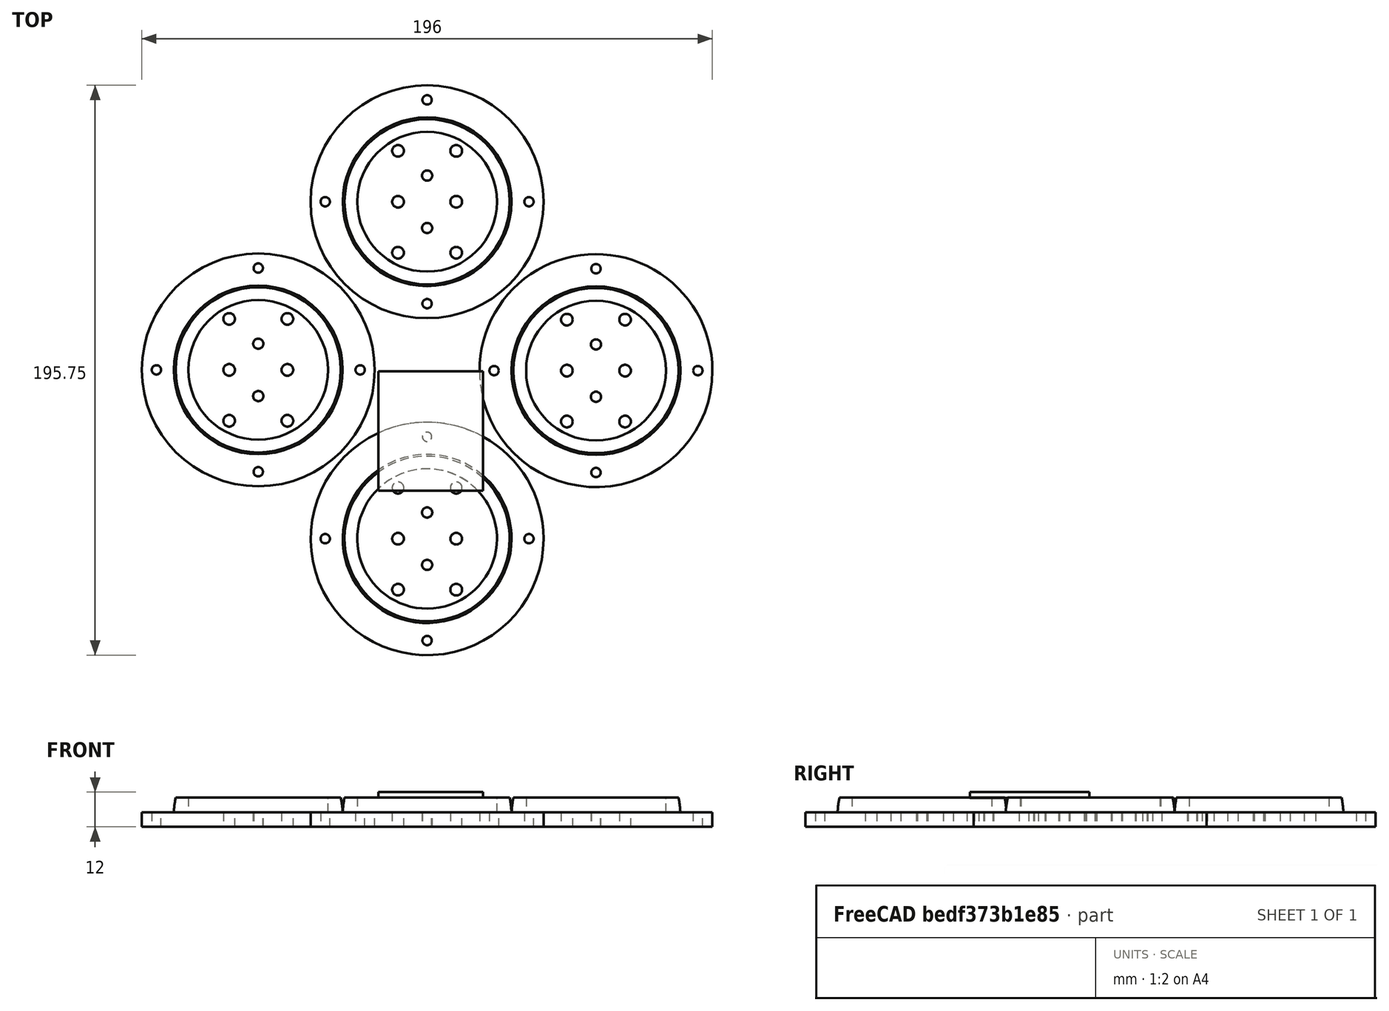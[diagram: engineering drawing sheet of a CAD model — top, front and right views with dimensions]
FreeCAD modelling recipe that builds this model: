
FCSTD DOCUMENT  (FreeCAD 0.20R29410 (Git))
Label: lightModuleV2
License: All rights reserved
LicenseURL: http://en.wikipedia.org/wiki/All_rights_reserved
objects: Part::Cylinder×56, Part::MultiFuse×32, Part::Cut×12, Part::Sphere×4, Mesh::Feature×1, Sketcher::SketchObject×1, Part::Box×1
note: 106 computed .brp shape members not serialized (recipe doc carries the construction recipe); baked Part::Feature solids carry a one-line shape summary decoded from their .brp

FEATURE [Mesh::Feature] Odroid_H004  label="Odroid-H004"
FEATURE [Sketcher::SketchObject] Sketch  label="top"
  FullyConstrained = false
  sketch-geometry (25):
    g0: Circle CenterX=0 CenterY=-150 CenterZ=0 NormalX=0 NormalY=0 NormalZ=1 AngleXU=0 Radius=100
    g1: Circle CenterX=0 CenterY=-208 CenterZ=0 NormalX=0 NormalY=0 NormalZ=1 AngleXU=0 Radius=40
    g2: Circle CenterX=58 CenterY=-150 CenterZ=0 NormalX=0 NormalY=0 NormalZ=1 AngleXU=0 Radius=40
    g3: Circle CenterX=0 CenterY=-92 CenterZ=0 NormalX=0 NormalY=0 NormalZ=1 AngleXU=0 Radius=40
    g4: Circle CenterX=-58 CenterY=-150 CenterZ=0 NormalX=0 NormalY=0 NormalZ=1 AngleXU=0 Radius=40
    g5: Circle CenterX=-93.2591 CenterY=-150.487 CenterZ=0 NormalX=0 NormalY=0 NormalZ=1 AngleXU=0 Radius=1.31835
    g6: Circle CenterX=-57.3054 CenterY=-115.377 CenterZ=0 NormalX=0 NormalY=0 NormalZ=1 AngleXU=0 Radius=2.19437
    g7: Circle CenterX=-22.8708 CenterY=-149.812 CenterZ=0 NormalX=0 NormalY=0 NormalZ=1 AngleXU=0 Radius=2.50935
    g8: Circle CenterX=-58.3181 CenterY=-186.103 CenterZ=0 NormalX=0 NormalY=0 NormalZ=1 AngleXU=0 Radius=1.8872
    g9: Circle CenterX=0 CenterY=-172.431 CenterZ=0 NormalX=0 NormalY=0 NormalZ=1 AngleXU=0 Radius=3.27743
    g10: Circle CenterX=0 CenterY=-243.157 CenterZ=0 NormalX=0 NormalY=0 NormalZ=1 AngleXU=0 Radius=1.88719
    g11: Circle CenterX=-35.1929 CenterY=-208.216 CenterZ=0 NormalX=0 NormalY=0 NormalZ=1 AngleXU=0 Radius=2.03259
    g12: Circle CenterX=35.7018 CenterY=-208.047 CenterZ=0 NormalX=0 NormalY=0 NormalZ=1 AngleXU=0 Radius=2.06044
    g13: Circle CenterX=57.8865 CenterY=-185.172 CenterZ=0 NormalX=0 NormalY=0 NormalZ=1 AngleXU=0 Radius=1.98371
    g14: Circle CenterX=23.2953 CenterY=-150.097 CenterZ=0 NormalX=0 NormalY=0 NormalZ=1 AngleXU=0 Radius=1.91236
    g15: Circle CenterX=58.0074 CenterY=-115.385 CenterZ=0 NormalX=0 NormalY=0 NormalZ=1 AngleXU=0 Radius=2.56571
    g16: Circle CenterX=93.3244 CenterY=-150.823 CenterZ=0 NormalX=0 NormalY=0 NormalZ=1 AngleXU=0 Radius=1.84224
    g17: Circle CenterX=0 CenterY=-58.0915 CenterZ=0 NormalX=0 NormalY=0 NormalZ=1 AngleXU=0 Radius=2.47929
    g18: Circle CenterX=0 CenterY=-208 CenterZ=0 NormalX=0 NormalY=0 NormalZ=1 AngleXU=0 Radius=25.6697
    g19: Circle CenterX=-58 CenterY=-150 CenterZ=0 NormalX=0 NormalY=0 NormalZ=1 AngleXU=0 Radius=24.6603
    g20: Circle CenterX=58 CenterY=-150 CenterZ=0 NormalX=0 NormalY=0 NormalZ=1 AngleXU=0 Radius=24.7378
    g21: Circle CenterX=0 CenterY=-92 CenterZ=0 NormalX=0 NormalY=0 NormalZ=1 AngleXU=0 Radius=24.1932
    g22: Circle CenterX=-35.0038 CenterY=-92.3918 CenterZ=0 NormalX=0 NormalY=0 NormalZ=1 AngleXU=0 Radius=2.19456
    g23: Circle CenterX=34.6146 CenterY=-92.5741 CenterZ=0 NormalX=0 NormalY=0 NormalZ=1 AngleXU=0 Radius=1.93732
    g24: Circle CenterX=0 CenterY=-127.201 CenterZ=0 NormalX=0 NormalY=0 NormalZ=1 AngleXU=0 Radius=2.07794
  constraints (23):
    c: PointOnObject(g0,g-2)
    c: Radius(g0) = 100
    c: DistanceY(g0) = -150
    c: PointOnObject(g1,g-2)
    c: PointOnObject(g3,g-2)
    c: DistanceY(g0,g2) = 0
    c: DistanceY(g0,g4) = 0
    c: DistanceY(g1,g0) = 58
    c: DistanceX(g4,g0) = 58
    c: DistanceX(g0,g2) = 58
    c: DistanceY(g0,g3) = 58
    c: Equal(g1,g2)
    c: Equal(g1,g3)
    c: Equal(g1,g4)
    c: Radius(g1) = 40
    c: PointOnObject(g9,g-2)
    c: PointOnObject(g10,g-2)
    c: PointOnObject(g17,g-2)
    c: Coincident(g18,g1)
    c: Coincident(g19,g4)
    c: Coincident(g20,g2)
    c: Coincident(g21,g3)
    c: PointOnObject(g24,g-2)
FEATURE [Part::Cylinder] Cylinder036
  Angle = 360
  AttacherType = Attacher::AttachEngine3D
  FirstAngle = 0
  Height = 10
  Placement = pos=(0,-21,0) rot=(0,0,1;0rad)
  Radius = 2
  SecondAngle = 0
FEATURE [Part::Cylinder] Cylinder037
  Angle = 360
  AttacherType = Attacher::AttachEngine3D
  FirstAngle = 0
  Height = 10
  Placement = pos=(20,-21,0) rot=(0,0,1;0rad)
  Radius = 2
  SecondAngle = 0
FEATURE [Part::Cylinder] Cylinder038
  Angle = 360
  AttacherType = Attacher::AttachEngine3D
  FirstAngle = 0
  Height = 10
  Placement = pos=(0,-21,0) rot=(0,0,1;0rad)
  Radius = 2
  SecondAngle = 0
FEATURE [Part::Cylinder] Cylinder039
  Angle = 360
  AttacherType = Attacher::AttachEngine3D
  FirstAngle = 0
  Height = 10
  Placement = pos=(20,-21,0) rot=(0,0,1;0rad)
  Radius = 2
  SecondAngle = 0
FEATURE [Part::Cylinder] Cylinder040  label="base002"
  Angle = 360
  AttacherType = Attacher::AttachEngine3D
  FirstAngle = 0
  Height = 5
  Placement = pos=(5,0,70) rot=(0,0,1;0rad)
  Radius = 40
  SecondAngle = 0
FEATURE [Part::Cylinder] Cylinder041  label="baseCut001"
  Angle = 360
  AttacherType = Attacher::AttachEngine3D
  FirstAngle = 0
  Height = 7
  Placement = pos=(5,0,74) rot=(0,0,1;0rad)
  Radius = 24
  SecondAngle = 0
FEATURE [Part::Cylinder] Cylinder042  label="wireCUt002"
  Angle = 360
  AttacherType = Attacher::AttachEngine3D
  FirstAngle = 0
  Height = 10
  Placement = pos=(-5,0,70) rot=(0,0,1;0rad)
  Radius = 2
  SecondAngle = 0
FEATURE [Part::Cylinder] Cylinder043  label="wireCUt003"
  Angle = 360
  AttacherType = Attacher::AttachEngine3D
  FirstAngle = 0
  Height = 10
  Placement = pos=(15,0,70) rot=(0,0,1;0rad)
  Radius = 2
  SecondAngle = 0
FEATURE [Part::Cylinder] Cylinder044  label="m3Cuts002"
  Angle = 360
  AttacherType = Attacher::AttachEngine3D
  FirstAngle = 0
  Height = 10
  Placement = pos=(5,-9,70) rot=(0,0,1;0rad)
  Radius = 1.75
  SecondAngle = 0
FEATURE [Part::Cylinder] Cylinder045  label="m3Cuts003"
  Angle = 360
  AttacherType = Attacher::AttachEngine3D
  FirstAngle = 0
  Height = 10
  Placement = pos=(5,9,70) rot=(0,0,1;0rad)
  Radius = 1.75
  SecondAngle = 0
FEATURE [Part::Cylinder] Cylinder046  label="m2HeatSetInsets004"
  Angle = 360
  AttacherType = Attacher::AttachEngine3D
  FirstAngle = 0
  Height = 10
  Placement = pos=(-30,0,65) rot=(0,0,1;0rad)
  Radius = 1.6
  SecondAngle = 0
FEATURE [Part::Cylinder] Cylinder047  label="m2HeatSetInsets005"
  Angle = 360
  AttacherType = Attacher::AttachEngine3D
  FirstAngle = 0
  Height = 10
  Placement = pos=(40,0,65) rot=(0,0,1;0rad)
  Radius = 1.6
  SecondAngle = 0
FEATURE [Part::Cylinder] Cylinder048  label="m2HeatSetInsets006"
  Angle = 360
  AttacherType = Attacher::AttachEngine3D
  FirstAngle = 0
  Height = 10
  Placement = pos=(5,35,65) rot=(0,0,1;0rad)
  Radius = 1.6
  SecondAngle = 0
FEATURE [Part::Cylinder] Cylinder049  label="m2HeatSetInsets007"
  Angle = 360
  AttacherType = Attacher::AttachEngine3D
  FirstAngle = 0
  Height = 10
  Placement = pos=(5,-35,65) rot=(0,0,1;0rad)
  Radius = 1.6
  SecondAngle = 0
FEATURE [Part::MultiFuse] Fusion014  label="m3HeatSetCuts003"
  Placement = pos=(-5,38.5,70) rot=(0,0,1;0rad)
  Shapes = -> [Cylinder037,Cylinder036]
FEATURE [Part::MultiFuse] Fusion015  label="m3HeatSetCuts004"
  Placement = pos=(-5,3.5,70) rot=(0,0,1;0rad)
  Shapes = -> [Cylinder039,Cylinder038]
FEATURE [Part::MultiFuse] Fusion016  label="m3HeatSetCuts005"
  Shapes = -> [Fusion015,Fusion014]
FEATURE [Part::MultiFuse] Fusion017  label="wireCuts001"
  Shapes = -> [Cylinder042,Cylinder043]
FEATURE [Part::MultiFuse] Fusion018  label="m3Cute001"
  Shapes = -> [Cylinder044,Cylinder045]
FEATURE [Part::MultiFuse] Fusion019  label="baseCUts001"
  Shapes = -> [Fusion016,Fusion017,Fusion018]
FEATURE [Part::MultiFuse] Fusion021
  Shapes = -> [Cylinder046,Cylinder047,Cylinder048,Cylinder049]
FEATURE [Part::Sphere] Sphere002  label="SphereBase001"
  Angle1 = 0
  Angle2 = 12
  Angle3 = 360
  AttacherType = Attacher::AttachEngine3D
  Placement = pos=(5,0,74) rot=(0,0,1;0rad)
  Radius = 29
FEATURE [Part::Cut] Cut006
  Base = -> Sphere002
  Tool = -> Cylinder041
FEATURE [Part::MultiFuse] Fusion020  label="base003"
  Shapes = -> [Cylinder040,Cut006]
FEATURE [Part::Cut] Cut007
  Base = -> Fusion020
  Tool = -> Fusion019
FEATURE [Part::Cut] Cut008  label="lightModule001"
  Base = -> Cut007
  Placement = pos=(-5,-208,0) rot=(0,1,0;0rad)
  Tool = -> Fusion021
FEATURE [Part::Box] Box005  label="as7265x"
  AttacherType = Attacher::AttachEngine3D
  Height = 2
  Length = 36
  Placement = pos=(-16.75,-191.5,80) rot=(0,0,1;0rad)
  Width = 41
FEATURE [Part::Cylinder] Cylinder050
  Angle = 360
  AttacherType = Attacher::AttachEngine3D
  FirstAngle = 0
  Height = 10
  Placement = pos=(0,-21,0) rot=(0,0,1;0rad)
  Radius = 2
  SecondAngle = 0
FEATURE [Part::Cylinder] Cylinder051
  Angle = 360
  AttacherType = Attacher::AttachEngine3D
  FirstAngle = 0
  Height = 10
  Placement = pos=(20,-21,0) rot=(0,0,1;0rad)
  Radius = 2
  SecondAngle = 0
FEATURE [Part::Cylinder] Cylinder052
  Angle = 360
  AttacherType = Attacher::AttachEngine3D
  FirstAngle = 0
  Height = 10
  Placement = pos=(0,-21,0) rot=(0,0,1;0rad)
  Radius = 2
  SecondAngle = 0
FEATURE [Part::Cylinder] Cylinder053
  Angle = 360
  AttacherType = Attacher::AttachEngine3D
  FirstAngle = 0
  Height = 10
  Placement = pos=(20,-21,0) rot=(0,0,1;0rad)
  Radius = 2
  SecondAngle = 0
FEATURE [Part::Cylinder] Cylinder054  label="base004"
  Angle = 360
  AttacherType = Attacher::AttachEngine3D
  FirstAngle = 0
  Height = 5
  Placement = pos=(5,0,70) rot=(0,0,1;0rad)
  Radius = 40
  SecondAngle = 0
FEATURE [Part::Cylinder] Cylinder055  label="baseCut002"
  Angle = 360
  AttacherType = Attacher::AttachEngine3D
  FirstAngle = 0
  Height = 7
  Placement = pos=(5,0,74) rot=(0,0,1;0rad)
  Radius = 24
  SecondAngle = 0
FEATURE [Part::Cylinder] Cylinder056  label="wireCUt004"
  Angle = 360
  AttacherType = Attacher::AttachEngine3D
  FirstAngle = 0
  Height = 10
  Placement = pos=(-5,0,70) rot=(0,0,1;0rad)
  Radius = 2
  SecondAngle = 0
FEATURE [Part::Cylinder] Cylinder057  label="wireCUt005"
  Angle = 360
  AttacherType = Attacher::AttachEngine3D
  FirstAngle = 0
  Height = 10
  Placement = pos=(15,0,70) rot=(0,0,1;0rad)
  Radius = 2
  SecondAngle = 0
FEATURE [Part::Cylinder] Cylinder058  label="m3Cuts004"
  Angle = 360
  AttacherType = Attacher::AttachEngine3D
  FirstAngle = 0
  Height = 10
  Placement = pos=(5,-9,70) rot=(0,0,1;0rad)
  Radius = 1.75
  SecondAngle = 0
FEATURE [Part::Cylinder] Cylinder059  label="m3Cuts005"
  Angle = 360
  AttacherType = Attacher::AttachEngine3D
  FirstAngle = 0
  Height = 10
  Placement = pos=(5,9,70) rot=(0,0,1;0rad)
  Radius = 1.75
  SecondAngle = 0
FEATURE [Part::Cylinder] Cylinder060  label="m2HeatSetInsets008"
  Angle = 360
  AttacherType = Attacher::AttachEngine3D
  FirstAngle = 0
  Height = 10
  Placement = pos=(-30,0,65) rot=(0,0,1;0rad)
  Radius = 1.6
  SecondAngle = 0
FEATURE [Part::Cylinder] Cylinder061  label="m2HeatSetInsets009"
  Angle = 360
  AttacherType = Attacher::AttachEngine3D
  FirstAngle = 0
  Height = 10
  Placement = pos=(40,0,65) rot=(0,0,1;0rad)
  Radius = 1.6
  SecondAngle = 0
FEATURE [Part::Cylinder] Cylinder062  label="m2HeatSetInsets010"
  Angle = 360
  AttacherType = Attacher::AttachEngine3D
  FirstAngle = 0
  Height = 10
  Placement = pos=(5,35,65) rot=(0,0,1;0rad)
  Radius = 1.6
  SecondAngle = 0
FEATURE [Part::Cylinder] Cylinder063  label="m2HeatSetInsets011"
  Angle = 360
  AttacherType = Attacher::AttachEngine3D
  FirstAngle = 0
  Height = 10
  Placement = pos=(5,-35,65) rot=(0,0,1;0rad)
  Radius = 1.6
  SecondAngle = 0
FEATURE [Part::MultiFuse] Fusion022  label="m3HeatSetCuts006"
  Placement = pos=(-5,38.5,70) rot=(0,0,1;0rad)
  Shapes = -> [Cylinder051,Cylinder050]
FEATURE [Part::MultiFuse] Fusion023  label="m3HeatSetCuts007"
  Placement = pos=(-5,3.5,70) rot=(0,0,1;0rad)
  Shapes = -> [Cylinder053,Cylinder052]
FEATURE [Part::MultiFuse] Fusion024  label="m3HeatSetCuts008"
  Shapes = -> [Fusion023,Fusion022]
FEATURE [Part::MultiFuse] Fusion025  label="wireCuts002"
  Shapes = -> [Cylinder056,Cylinder057]
FEATURE [Part::MultiFuse] Fusion026  label="m3Cute002"
  Shapes = -> [Cylinder058,Cylinder059]
FEATURE [Part::MultiFuse] Fusion027  label="baseCUts002"
  Shapes = -> [Fusion024,Fusion025,Fusion026]
FEATURE [Part::MultiFuse] Fusion029
  Shapes = -> [Cylinder060,Cylinder061,Cylinder062,Cylinder063]
FEATURE [Part::Sphere] Sphere003  label="SphereBase002"
  Angle1 = 0
  Angle2 = 12
  Angle3 = 360
  AttacherType = Attacher::AttachEngine3D
  Placement = pos=(5,0,74) rot=(0,0,1;0rad)
  Radius = 29
FEATURE [Part::Cut] Cut009
  Base = -> Sphere003
  Tool = -> Cylinder055
FEATURE [Part::MultiFuse] Fusion028  label="base005"
  Shapes = -> [Cylinder054,Cut009]
FEATURE [Part::Cut] Cut010
  Base = -> Fusion028
  Tool = -> Fusion027
FEATURE [Part::Cut] Cut011  label="lightModule002"
  Base = -> Cut010
  Placement = pos=(-63,-150,0) rot=(0,1,0;0rad)
  Tool = -> Fusion029
FEATURE [Part::Cylinder] Cylinder064
  Angle = 360
  AttacherType = Attacher::AttachEngine3D
  FirstAngle = 0
  Height = 10
  Placement = pos=(0,-21,0) rot=(0,0,1;0rad)
  Radius = 2
  SecondAngle = 0
FEATURE [Part::Cylinder] Cylinder065
  Angle = 360
  AttacherType = Attacher::AttachEngine3D
  FirstAngle = 0
  Height = 10
  Placement = pos=(20,-21,0) rot=(0,0,1;0rad)
  Radius = 2
  SecondAngle = 0
FEATURE [Part::Cylinder] Cylinder066
  Angle = 360
  AttacherType = Attacher::AttachEngine3D
  FirstAngle = 0
  Height = 10
  Placement = pos=(0,-21,0) rot=(0,0,1;0rad)
  Radius = 2
  SecondAngle = 0
FEATURE [Part::Cylinder] Cylinder067
  Angle = 360
  AttacherType = Attacher::AttachEngine3D
  FirstAngle = 0
  Height = 10
  Placement = pos=(20,-21,0) rot=(0,0,1;0rad)
  Radius = 2
  SecondAngle = 0
FEATURE [Part::Cylinder] Cylinder068  label="base006"
  Angle = 360
  AttacherType = Attacher::AttachEngine3D
  FirstAngle = 0
  Height = 5
  Placement = pos=(5,0,70) rot=(0,0,1;0rad)
  Radius = 40
  SecondAngle = 0
FEATURE [Part::Cylinder] Cylinder069  label="baseCut003"
  Angle = 360
  AttacherType = Attacher::AttachEngine3D
  FirstAngle = 0
  Height = 7
  Placement = pos=(5,0,74) rot=(0,0,1;0rad)
  Radius = 24
  SecondAngle = 0
FEATURE [Part::Cylinder] Cylinder070  label="wireCUt006"
  Angle = 360
  AttacherType = Attacher::AttachEngine3D
  FirstAngle = 0
  Height = 10
  Placement = pos=(-5,0,70) rot=(0,0,1;0rad)
  Radius = 2
  SecondAngle = 0
FEATURE [Part::Cylinder] Cylinder071  label="wireCUt007"
  Angle = 360
  AttacherType = Attacher::AttachEngine3D
  FirstAngle = 0
  Height = 10
  Placement = pos=(15,0,70) rot=(0,0,1;0rad)
  Radius = 2
  SecondAngle = 0
FEATURE [Part::Cylinder] Cylinder072  label="m3Cuts006"
  Angle = 360
  AttacherType = Attacher::AttachEngine3D
  FirstAngle = 0
  Height = 10
  Placement = pos=(5,-9,70) rot=(0,0,1;0rad)
  Radius = 1.75
  SecondAngle = 0
FEATURE [Part::Cylinder] Cylinder073  label="m3Cuts007"
  Angle = 360
  AttacherType = Attacher::AttachEngine3D
  FirstAngle = 0
  Height = 10
  Placement = pos=(5,9,70) rot=(0,0,1;0rad)
  Radius = 1.75
  SecondAngle = 0
FEATURE [Part::Cylinder] Cylinder074  label="m2HeatSetInsets012"
  Angle = 360
  AttacherType = Attacher::AttachEngine3D
  FirstAngle = 0
  Height = 10
  Placement = pos=(-30,0,65) rot=(0,0,1;0rad)
  Radius = 1.6
  SecondAngle = 0
FEATURE [Part::Cylinder] Cylinder075  label="m2HeatSetInsets013"
  Angle = 360
  AttacherType = Attacher::AttachEngine3D
  FirstAngle = 0
  Height = 10
  Placement = pos=(40,0,65) rot=(0,0,1;0rad)
  Radius = 1.6
  SecondAngle = 0
FEATURE [Part::Cylinder] Cylinder076  label="m2HeatSetInsets014"
  Angle = 360
  AttacherType = Attacher::AttachEngine3D
  FirstAngle = 0
  Height = 10
  Placement = pos=(5,35,65) rot=(0,0,1;0rad)
  Radius = 1.6
  SecondAngle = 0
FEATURE [Part::Cylinder] Cylinder077  label="m2HeatSetInsets015"
  Angle = 360
  AttacherType = Attacher::AttachEngine3D
  FirstAngle = 0
  Height = 10
  Placement = pos=(5,-35,65) rot=(0,0,1;0rad)
  Radius = 1.6
  SecondAngle = 0
FEATURE [Part::MultiFuse] Fusion030  label="m3HeatSetCuts009"
  Placement = pos=(-5,38.5,70) rot=(0,0,1;0rad)
  Shapes = -> [Cylinder065,Cylinder064]
FEATURE [Part::MultiFuse] Fusion031  label="m3HeatSetCuts010"
  Placement = pos=(-5,3.5,70) rot=(0,0,1;0rad)
  Shapes = -> [Cylinder067,Cylinder066]
FEATURE [Part::MultiFuse] Fusion032  label="m3HeatSetCuts011"
  Shapes = -> [Fusion031,Fusion030]
FEATURE [Part::MultiFuse] Fusion033  label="wireCuts003"
  Shapes = -> [Cylinder070,Cylinder071]
FEATURE [Part::MultiFuse] Fusion034  label="m3Cute003"
  Shapes = -> [Cylinder072,Cylinder073]
FEATURE [Part::MultiFuse] Fusion035  label="baseCUts003"
  Shapes = -> [Fusion032,Fusion033,Fusion034]
FEATURE [Part::MultiFuse] Fusion037
  Shapes = -> [Cylinder074,Cylinder075,Cylinder076,Cylinder077]
FEATURE [Part::Sphere] Sphere004  label="SphereBase003"
  Angle1 = 0
  Angle2 = 12
  Angle3 = 360
  AttacherType = Attacher::AttachEngine3D
  Placement = pos=(5,0,74) rot=(0,0,1;0rad)
  Radius = 29
FEATURE [Part::Cut] Cut012
  Base = -> Sphere004
  Tool = -> Cylinder069
FEATURE [Part::MultiFuse] Fusion036  label="base007"
  Shapes = -> [Cylinder068,Cut012]
FEATURE [Part::Cut] Cut013
  Base = -> Fusion036
  Tool = -> Fusion035
FEATURE [Part::Cut] Cut014  label="lightModule003"
  Base = -> Cut013
  Placement = pos=(53,-150.25,0) rot=(0,1,0;0rad)
  Tool = -> Fusion037
FEATURE [Part::Cylinder] Cylinder078
  Angle = 360
  AttacherType = Attacher::AttachEngine3D
  FirstAngle = 0
  Height = 10
  Placement = pos=(0,-21,0) rot=(0,0,1;0rad)
  Radius = 2
  SecondAngle = 0
FEATURE [Part::Cylinder] Cylinder079
  Angle = 360
  AttacherType = Attacher::AttachEngine3D
  FirstAngle = 0
  Height = 10
  Placement = pos=(20,-21,0) rot=(0,0,1;0rad)
  Radius = 2
  SecondAngle = 0
FEATURE [Part::Cylinder] Cylinder080
  Angle = 360
  AttacherType = Attacher::AttachEngine3D
  FirstAngle = 0
  Height = 10
  Placement = pos=(0,-21,0) rot=(0,0,1;0rad)
  Radius = 2
  SecondAngle = 0
FEATURE [Part::Cylinder] Cylinder081
  Angle = 360
  AttacherType = Attacher::AttachEngine3D
  FirstAngle = 0
  Height = 10
  Placement = pos=(20,-21,0) rot=(0,0,1;0rad)
  Radius = 2
  SecondAngle = 0
FEATURE [Part::Cylinder] Cylinder082  label="base008"
  Angle = 360
  AttacherType = Attacher::AttachEngine3D
  FirstAngle = 0
  Height = 5
  Placement = pos=(5,0,70) rot=(0,0,1;0rad)
  Radius = 40
  SecondAngle = 0
FEATURE [Part::Cylinder] Cylinder083  label="baseCut004"
  Angle = 360
  AttacherType = Attacher::AttachEngine3D
  FirstAngle = 0
  Height = 7
  Placement = pos=(5,0,74) rot=(0,0,1;0rad)
  Radius = 24
  SecondAngle = 0
FEATURE [Part::Cylinder] Cylinder084  label="wireCUt008"
  Angle = 360
  AttacherType = Attacher::AttachEngine3D
  FirstAngle = 0
  Height = 10
  Placement = pos=(-5,0,70) rot=(0,0,1;0rad)
  Radius = 2
  SecondAngle = 0
FEATURE [Part::Cylinder] Cylinder085  label="wireCUt009"
  Angle = 360
  AttacherType = Attacher::AttachEngine3D
  FirstAngle = 0
  Height = 10
  Placement = pos=(15,0,70) rot=(0,0,1;0rad)
  Radius = 2
  SecondAngle = 0
FEATURE [Part::Cylinder] Cylinder086  label="m3Cuts008"
  Angle = 360
  AttacherType = Attacher::AttachEngine3D
  FirstAngle = 0
  Height = 10
  Placement = pos=(5,-9,70) rot=(0,0,1;0rad)
  Radius = 1.75
  SecondAngle = 0
FEATURE [Part::Cylinder] Cylinder087  label="m3Cuts009"
  Angle = 360
  AttacherType = Attacher::AttachEngine3D
  FirstAngle = 0
  Height = 10
  Placement = pos=(5,9,70) rot=(0,0,1;0rad)
  Radius = 1.75
  SecondAngle = 0
FEATURE [Part::Cylinder] Cylinder088  label="m2HeatSetInsets016"
  Angle = 360
  AttacherType = Attacher::AttachEngine3D
  FirstAngle = 0
  Height = 10
  Placement = pos=(-30,0,65) rot=(0,0,1;0rad)
  Radius = 1.6
  SecondAngle = 0
FEATURE [Part::Cylinder] Cylinder089  label="m2HeatSetInsets017"
  Angle = 360
  AttacherType = Attacher::AttachEngine3D
  FirstAngle = 0
  Height = 10
  Placement = pos=(40,0,65) rot=(0,0,1;0rad)
  Radius = 1.6
  SecondAngle = 0
FEATURE [Part::Cylinder] Cylinder090  label="m2HeatSetInsets018"
  Angle = 360
  AttacherType = Attacher::AttachEngine3D
  FirstAngle = 0
  Height = 10
  Placement = pos=(5,35,65) rot=(0,0,1;0rad)
  Radius = 1.6
  SecondAngle = 0
FEATURE [Part::Cylinder] Cylinder091  label="m2HeatSetInsets019"
  Angle = 360
  AttacherType = Attacher::AttachEngine3D
  FirstAngle = 0
  Height = 10
  Placement = pos=(5,-35,65) rot=(0,0,1;0rad)
  Radius = 1.6
  SecondAngle = 0
FEATURE [Part::MultiFuse] Fusion038  label="m3HeatSetCuts012"
  Placement = pos=(-5,38.5,70) rot=(0,0,1;0rad)
  Shapes = -> [Cylinder079,Cylinder078]
FEATURE [Part::MultiFuse] Fusion039  label="m3HeatSetCuts013"
  Placement = pos=(-5,3.5,70) rot=(0,0,1;0rad)
  Shapes = -> [Cylinder081,Cylinder080]
FEATURE [Part::MultiFuse] Fusion040  label="m3HeatSetCuts014"
  Shapes = -> [Fusion039,Fusion038]
FEATURE [Part::MultiFuse] Fusion041  label="wireCuts004"
  Shapes = -> [Cylinder084,Cylinder085]
FEATURE [Part::MultiFuse] Fusion042  label="m3Cute004"
  Shapes = -> [Cylinder086,Cylinder087]
FEATURE [Part::MultiFuse] Fusion043  label="baseCUts004"
  Shapes = -> [Fusion040,Fusion041,Fusion042]
FEATURE [Part::MultiFuse] Fusion045
  Shapes = -> [Cylinder088,Cylinder089,Cylinder090,Cylinder091]
FEATURE [Part::Sphere] Sphere005  label="SphereBase004"
  Angle1 = 0
  Angle2 = 12
  Angle3 = 360
  AttacherType = Attacher::AttachEngine3D
  Placement = pos=(5,0,74) rot=(0,0,1;0rad)
  Radius = 29
FEATURE [Part::Cut] Cut015
  Base = -> Sphere005
  Tool = -> Cylinder083
FEATURE [Part::MultiFuse] Fusion044  label="base009"
  Shapes = -> [Cylinder082,Cut015]
FEATURE [Part::Cut] Cut016
  Base = -> Fusion044
  Tool = -> Fusion043
FEATURE [Part::Cut] Cut017  label="lightModule004"
  Base = -> Cut016
  Placement = pos=(-5,-92.25,0) rot=(0,1,0;0rad)
  Tool = -> Fusion045
